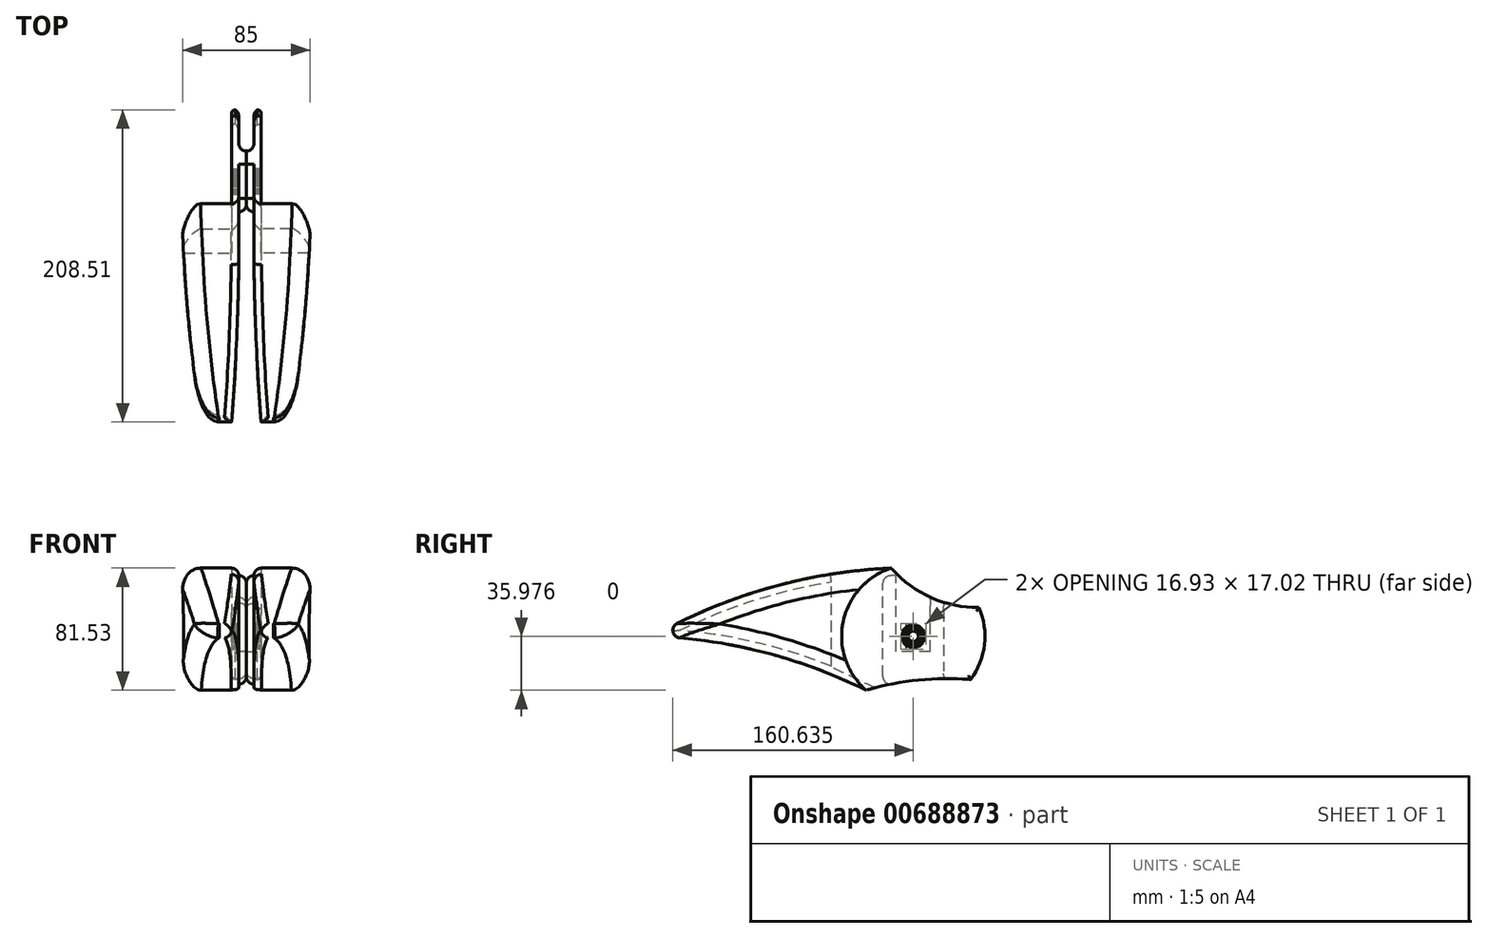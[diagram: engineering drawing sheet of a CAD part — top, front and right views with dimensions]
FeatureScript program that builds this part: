
annotation { "Feature Type Name" : "Feature", "Feature Type Description" : "" }
export const myFeature = defineFeature(function(context is Context, id is Id, definition is map)
    precondition{}
    {
        {
            var Q0;
            Q0=qCreatedBy(makeId("Right.planeOp"),FACE);
            var sketch = newSketch(context, id + "F0", { "sketchPlane" : qUnion([Q0])});
            skArc(sketch, "E0.0", {"start": v(-15.25, 45.51) * mm, "mid": v(-47.42, 9.65) * mm, "end": v(-32.12, -36.02) * mm});
            skArc(sketch, "E1", {"start": v(-15.25, 45.51) * mm, "mid": v(-97.5, 32.14) * mm, "end": v(-174.4, 0) * mm});
            skArc(sketch, "E2", {"start": v(-32.12, -36.02) * mm, "mid": v(-101.34, -10.43) * mm, "end": v(-174.4, 0) * mm});
            skArc(sketch, "E3", {"start": v(37.7, -28.86) * mm, "mid": v(2.47, -29.33) * mm, "end": v(-32.12, -36.02) * mm});
            skArc(sketch, "E4", {"start": v(-15.25, 45.51) * mm, "mid": v(11.16, 25.94) * mm, "end": v(43.33, 19.14) * mm});
            skArc(sketch, "E5.trimOffspring", {"start": v(37.7, -28.86) * mm, "mid": v(47.01, -5.62) * mm, "end": v(43.33, 19.14) * mm});
            skCircle(sketch, "E6", {"center": v(-0.54, -0.04) * mm, "radius": 3.43 * mm});
            skLineSegment(sketch, "E7", {"start": v(-0.54, -0.04) * mm, "end": v(-0.54, 10.9) * mm, "construction": true});
            skLineSegment(sketch, "E8.bottom", {"start": v(-0.55, 3.38) * mm, "end": v(-0.52, 3.38) * mm});
            skLineSegment(sketch, "E8.top", {"start": v(-0.55, 8.46) * mm, "end": v(-0.52, 8.46) * mm});
            skLineSegment(sketch, "E8.left", {"start": v(-0.55, 3.38) * mm, "end": v(-0.55, 8.46) * mm});
            skLineSegment(sketch, "E8.right", {"start": v(-0.52, 3.38) * mm, "end": v(-0.52, 8.46) * mm});
            skLineSegment(sketch, "E9.1.0", {"start": v(-1.24, 3.31) * mm, "end": v(-2.3, 8.28) * mm});
            skLineSegment(sketch, "E9.1.1", {"start": v(-1.26, 3.3) * mm, "end": v(-2.32, 8.28) * mm});
            skLineSegment(sketch, "E9.1.2", {"start": v(-2.32, 8.28) * mm, "end": v(-2.3, 8.28) * mm});
            skLineSegment(sketch, "E9.1.3", {"start": v(-1.26, 3.3) * mm, "end": v(-1.24, 3.31) * mm});
            skLineSegment(sketch, "E9.2.0", {"start": v(-1.92, 3.1) * mm, "end": v(-3.98, 7.73) * mm});
            skLineSegment(sketch, "E9.2.1", {"start": v(-1.94, 3.08) * mm, "end": v(-4, 7.72) * mm});
            skLineSegment(sketch, "E9.2.2", {"start": v(-4, 7.72) * mm, "end": v(-3.98, 7.73) * mm});
            skLineSegment(sketch, "E9.2.3", {"start": v(-1.94, 3.08) * mm, "end": v(-1.92, 3.1) * mm});
            skLineSegment(sketch, "E9.3.0", {"start": v(-2.54, 2.74) * mm, "end": v(-5.53, 6.85) * mm});
            skLineSegment(sketch, "E9.3.1", {"start": v(-2.56, 2.72) * mm, "end": v(-5.55, 6.83) * mm});
            skLineSegment(sketch, "E9.3.2", {"start": v(-5.55, 6.83) * mm, "end": v(-5.53, 6.85) * mm});
            skLineSegment(sketch, "E9.3.3", {"start": v(-2.56, 2.72) * mm, "end": v(-2.54, 2.74) * mm});
            skLineSegment(sketch, "E9.4.0", {"start": v(-3.08, 2.26) * mm, "end": v(-6.85, 5.66) * mm});
            skLineSegment(sketch, "E9.4.1", {"start": v(-3.1, 2.24) * mm, "end": v(-6.87, 5.64) * mm});
            skLineSegment(sketch, "E9.4.2", {"start": v(-6.87, 5.64) * mm, "end": v(-6.85, 5.66) * mm});
            skLineSegment(sketch, "E9.4.3", {"start": v(-3.1, 2.24) * mm, "end": v(-3.08, 2.26) * mm});
            skLineSegment(sketch, "E9.5.0", {"start": v(-3.5, 1.68) * mm, "end": v(-7.9, 4.22) * mm});
            skLineSegment(sketch, "E9.5.1", {"start": v(-3.51, 1.66) * mm, "end": v(-7.91, 4.2) * mm});
            skLineSegment(sketch, "E9.5.2", {"start": v(-7.91, 4.2) * mm, "end": v(-7.9, 4.22) * mm});
            skLineSegment(sketch, "E9.5.3", {"start": v(-3.51, 1.66) * mm, "end": v(-3.5, 1.68) * mm});
            skLineSegment(sketch, "E9.6.0", {"start": v(-3.8, 1.03) * mm, "end": v(-8.62, 2.6) * mm});
            skLineSegment(sketch, "E9.6.1", {"start": v(-3.8, 1) * mm, "end": v(-8.63, 2.57) * mm});
            skLineSegment(sketch, "E9.6.2", {"start": v(-8.63, 2.57) * mm, "end": v(-8.62, 2.6) * mm});
            skLineSegment(sketch, "E9.6.3", {"start": v(-3.8, 1) * mm, "end": v(-3.8, 1.03) * mm});
            skLineSegment(sketch, "E9.7.0", {"start": v(-3.94, 0.33) * mm, "end": v(-9, 0.86) * mm});
            skLineSegment(sketch, "E9.7.1", {"start": v(-3.95, 0.3) * mm, "end": v(-9, 0.83) * mm});
            skLineSegment(sketch, "E9.7.2", {"start": v(-9, 0.83) * mm, "end": v(-9, 0.86) * mm});
            skLineSegment(sketch, "E9.7.3", {"start": v(-3.95, 0.3) * mm, "end": v(-3.94, 0.33) * mm});
            skLineSegment(sketch, "E9.8.0", {"start": v(-3.95, -0.39) * mm, "end": v(-9, -0.92) * mm});
            skLineSegment(sketch, "E9.8.1", {"start": v(-3.94, -0.42) * mm, "end": v(-9, -0.95) * mm});
            skLineSegment(sketch, "E9.8.2", {"start": v(-9, -0.95) * mm, "end": v(-9, -0.92) * mm});
            skLineSegment(sketch, "E9.8.3", {"start": v(-3.94, -0.42) * mm, "end": v(-3.95, -0.39) * mm});
            skLineSegment(sketch, "E9.9.0", {"start": v(-3.8, -1.1) * mm, "end": v(-8.63, -2.66) * mm});
            skLineSegment(sketch, "E9.9.1", {"start": v(-3.8, -1.12) * mm, "end": v(-8.62, -2.69) * mm});
            skLineSegment(sketch, "E9.9.2", {"start": v(-8.62, -2.69) * mm, "end": v(-8.63, -2.66) * mm});
            skLineSegment(sketch, "E9.9.3", {"start": v(-3.8, -1.12) * mm, "end": v(-3.8, -1.1) * mm});
            skLineSegment(sketch, "E10.3.10.0", {"start": v(-3.5, -1.77) * mm, "end": v(-7.9, -4.3) * mm});
            skLineSegment(sketch, "E10.4.10.0", {"start": v(-3.51, -1.75) * mm, "end": v(-7.91, -4.29) * mm});
            skLineSegment(sketch, "E10.6.10.0", {"start": v(-7.9, -4.3) * mm, "end": v(-7.91, -4.29) * mm});
            skLineSegment(sketch, "E10.9.10.0", {"start": v(-3.5, -1.77) * mm, "end": v(-3.51, -1.75) * mm});
            skLineSegment(sketch, "E11.3.11.0", {"start": v(-3.08, -2.35) * mm, "end": v(-6.85, -5.75) * mm});
            skLineSegment(sketch, "E11.4.11.0", {"start": v(-3.1, -2.33) * mm, "end": v(-6.87, -5.73) * mm});
            skLineSegment(sketch, "E11.6.11.0", {"start": v(-6.85, -5.75) * mm, "end": v(-6.87, -5.73) * mm});
            skLineSegment(sketch, "E11.9.11.0", {"start": v(-3.08, -2.35) * mm, "end": v(-3.1, -2.33) * mm});
            skLineSegment(sketch, "E12.3.12.0", {"start": v(-2.54, -2.83) * mm, "end": v(-5.53, -6.94) * mm});
            skLineSegment(sketch, "E12.4.12.0", {"start": v(-2.56, -2.81) * mm, "end": v(-5.55, -6.92) * mm});
            skLineSegment(sketch, "E12.6.12.0", {"start": v(-5.53, -6.94) * mm, "end": v(-5.55, -6.92) * mm});
            skLineSegment(sketch, "E12.9.12.0", {"start": v(-2.54, -2.83) * mm, "end": v(-2.56, -2.81) * mm});
            skLineSegment(sketch, "E13.3.13.0", {"start": v(-1.92, -3.18) * mm, "end": v(-3.98, -7.82) * mm});
            skLineSegment(sketch, "E13.4.13.0", {"start": v(-1.94, -3.17) * mm, "end": v(-4, -7.81) * mm});
            skLineSegment(sketch, "E13.6.13.0", {"start": v(-3.98, -7.82) * mm, "end": v(-4, -7.81) * mm});
            skLineSegment(sketch, "E13.9.13.0", {"start": v(-1.92, -3.18) * mm, "end": v(-1.94, -3.17) * mm});
            skLineSegment(sketch, "E13.3.14.0", {"start": v(-1.24, -3.4) * mm, "end": v(-2.3, -8.37) * mm});
            skLineSegment(sketch, "E13.4.14.0", {"start": v(-1.26, -3.4) * mm, "end": v(-2.32, -8.36) * mm});
            skLineSegment(sketch, "E13.6.14.0", {"start": v(-2.3, -8.37) * mm, "end": v(-2.32, -8.36) * mm});
            skLineSegment(sketch, "E13.9.14.0", {"start": v(-1.24, -3.4) * mm, "end": v(-1.26, -3.4) * mm});
            skLineSegment(sketch, "E14.3.15.0", {"start": v(-0.52, -3.47) * mm, "end": v(-0.52, -8.55) * mm});
            skLineSegment(sketch, "E14.4.15.0", {"start": v(-0.55, -3.47) * mm, "end": v(-0.55, -8.55) * mm});
            skLineSegment(sketch, "E14.6.15.0", {"start": v(-0.52, -8.55) * mm, "end": v(-0.55, -8.55) * mm});
            skLineSegment(sketch, "E14.9.15.0", {"start": v(-0.52, -3.47) * mm, "end": v(-0.55, -3.47) * mm});
            skLineSegment(sketch, "E14.3.16.0", {"start": v(0.2, -3.4) * mm, "end": v(1.25, -8.36) * mm});
            skLineSegment(sketch, "E14.4.16.0", {"start": v(0.17, -3.4) * mm, "end": v(1.22, -8.37) * mm});
            skLineSegment(sketch, "E14.6.16.0", {"start": v(1.25, -8.36) * mm, "end": v(1.22, -8.37) * mm});
            skLineSegment(sketch, "E14.9.16.0", {"start": v(0.2, -3.4) * mm, "end": v(0.17, -3.4) * mm});
            skLineSegment(sketch, "E14.3.17.0", {"start": v(0.87, -3.17) * mm, "end": v(2.94, -7.81) * mm});
            skLineSegment(sketch, "E14.4.17.0", {"start": v(0.85, -3.18) * mm, "end": v(2.91, -7.82) * mm});
            skLineSegment(sketch, "E14.6.17.0", {"start": v(2.94, -7.81) * mm, "end": v(2.91, -7.82) * mm});
            skLineSegment(sketch, "E14.9.17.0", {"start": v(0.87, -3.17) * mm, "end": v(0.85, -3.18) * mm});
            skLineSegment(sketch, "E14.3.18.0", {"start": v(1.5, -2.81) * mm, "end": v(4.48, -6.92) * mm});
            skLineSegment(sketch, "E14.4.18.0", {"start": v(1.47, -2.83) * mm, "end": v(4.46, -6.94) * mm});
            skLineSegment(sketch, "E14.6.18.0", {"start": v(4.48, -6.92) * mm, "end": v(4.46, -6.94) * mm});
            skLineSegment(sketch, "E14.9.18.0", {"start": v(1.5, -2.81) * mm, "end": v(1.47, -2.83) * mm});
            skLineSegment(sketch, "E14.3.19.0", {"start": v(2.02, -2.33) * mm, "end": v(5.8, -5.73) * mm});
            skLineSegment(sketch, "E14.4.19.0", {"start": v(2, -2.35) * mm, "end": v(5.78, -5.75) * mm});
            skLineSegment(sketch, "E14.6.19.0", {"start": v(5.8, -5.73) * mm, "end": v(5.78, -5.75) * mm});
            skLineSegment(sketch, "E14.9.19.0", {"start": v(2.02, -2.33) * mm, "end": v(2, -2.35) * mm});
            skLineSegment(sketch, "E15.3.20.0", {"start": v(2.44, -1.75) * mm, "end": v(6.84, -4.29) * mm});
            skLineSegment(sketch, "E15.4.20.0", {"start": v(2.43, -1.77) * mm, "end": v(6.83, -4.3) * mm});
            skLineSegment(sketch, "E15.6.20.0", {"start": v(6.84, -4.29) * mm, "end": v(6.83, -4.3) * mm});
            skLineSegment(sketch, "E15.9.20.0", {"start": v(2.44, -1.75) * mm, "end": v(2.43, -1.77) * mm});
            skLineSegment(sketch, "E15.3.21.0", {"start": v(2.73, -1.1) * mm, "end": v(7.56, -2.66) * mm});
            skLineSegment(sketch, "E15.4.21.0", {"start": v(2.72, -1.12) * mm, "end": v(7.55, -2.69) * mm});
            skLineSegment(sketch, "E15.6.21.0", {"start": v(7.56, -2.66) * mm, "end": v(7.55, -2.69) * mm});
            skLineSegment(sketch, "E15.9.21.0", {"start": v(2.73, -1.1) * mm, "end": v(2.72, -1.12) * mm});
            skLineSegment(sketch, "E15.3.22.0", {"start": v(2.88, -0.39) * mm, "end": v(7.93, -0.92) * mm});
            skLineSegment(sketch, "E15.4.22.0", {"start": v(2.87, -0.42) * mm, "end": v(7.93, -0.95) * mm});
            skLineSegment(sketch, "E15.6.22.0", {"start": v(7.93, -0.92) * mm, "end": v(7.93, -0.95) * mm});
            skLineSegment(sketch, "E15.9.22.0", {"start": v(2.88, -0.39) * mm, "end": v(2.87, -0.42) * mm});
            skLineSegment(sketch, "E15.3.23.0", {"start": v(2.87, 0.33) * mm, "end": v(7.93, 0.86) * mm});
            skLineSegment(sketch, "E15.4.23.0", {"start": v(2.88, 0.3) * mm, "end": v(7.93, 0.83) * mm});
            skLineSegment(sketch, "E15.6.23.0", {"start": v(7.93, 0.86) * mm, "end": v(7.93, 0.83) * mm});
            skLineSegment(sketch, "E15.9.23.0", {"start": v(2.87, 0.33) * mm, "end": v(2.88, 0.3) * mm});
            skLineSegment(sketch, "E15.3.24.0", {"start": v(2.72, 1.03) * mm, "end": v(7.55, 2.6) * mm});
            skLineSegment(sketch, "E15.4.24.0", {"start": v(2.73, 1) * mm, "end": v(7.56, 2.57) * mm});
            skLineSegment(sketch, "E15.6.24.0", {"start": v(7.55, 2.6) * mm, "end": v(7.56, 2.57) * mm});
            skLineSegment(sketch, "E15.9.24.0", {"start": v(2.72, 1.03) * mm, "end": v(2.73, 1) * mm});
            skLineSegment(sketch, "E16.3.25.0", {"start": v(2.43, 1.68) * mm, "end": v(6.83, 4.22) * mm});
            skLineSegment(sketch, "E16.4.25.0", {"start": v(2.44, 1.66) * mm, "end": v(6.84, 4.2) * mm});
            skLineSegment(sketch, "E16.6.25.0", {"start": v(6.83, 4.22) * mm, "end": v(6.84, 4.2) * mm});
            skLineSegment(sketch, "E16.9.25.0", {"start": v(2.43, 1.68) * mm, "end": v(2.44, 1.66) * mm});
            skLineSegment(sketch, "E16.3.26.0", {"start": v(2, 2.26) * mm, "end": v(5.78, 5.66) * mm});
            skLineSegment(sketch, "E16.4.26.0", {"start": v(2.02, 2.24) * mm, "end": v(5.8, 5.64) * mm});
            skLineSegment(sketch, "E16.6.26.0", {"start": v(5.78, 5.66) * mm, "end": v(5.8, 5.64) * mm});
            skLineSegment(sketch, "E16.9.26.0", {"start": v(2, 2.26) * mm, "end": v(2.02, 2.24) * mm});
            skLineSegment(sketch, "E16.3.27.0", {"start": v(1.47, 2.74) * mm, "end": v(4.46, 6.85) * mm});
            skLineSegment(sketch, "E16.4.27.0", {"start": v(1.5, 2.72) * mm, "end": v(4.48, 6.83) * mm});
            skLineSegment(sketch, "E16.6.27.0", {"start": v(4.46, 6.85) * mm, "end": v(4.48, 6.83) * mm});
            skLineSegment(sketch, "E16.9.27.0", {"start": v(1.47, 2.74) * mm, "end": v(1.5, 2.72) * mm});
            skLineSegment(sketch, "E16.3.28.0", {"start": v(0.85, 3.1) * mm, "end": v(2.91, 7.73) * mm});
            skLineSegment(sketch, "E16.4.28.0", {"start": v(0.87, 3.08) * mm, "end": v(2.94, 7.72) * mm});
            skLineSegment(sketch, "E16.6.28.0", {"start": v(2.91, 7.73) * mm, "end": v(2.94, 7.72) * mm});
            skLineSegment(sketch, "E16.9.28.0", {"start": v(0.85, 3.1) * mm, "end": v(0.87, 3.08) * mm});
            skLineSegment(sketch, "E16.3.29.0", {"start": v(0.17, 3.31) * mm, "end": v(1.22, 8.28) * mm});
            skLineSegment(sketch, "E16.4.29.0", {"start": v(0.2, 3.3) * mm, "end": v(1.25, 8.28) * mm});
            skLineSegment(sketch, "E16.6.29.0", {"start": v(1.22, 8.28) * mm, "end": v(1.25, 8.28) * mm});
            skLineSegment(sketch, "E16.9.29.0", {"start": v(0.17, 3.31) * mm, "end": v(0.2, 3.3) * mm});
            skSolve(sketch);
        }
        {
            var Q0;
            Q0=makeQuery(id+"F0.imprint","IMPRINT",FACE,{"disambiguationData":[TD([[makeQuery(id+"F0.imprint","IMPRINT",EDGE,{"derivedFrom":sQuery(id+"F0.wireOp",EDGE,"E0.0")}),1.0]])]});
            extrude(context, id + "F1", {"entities" : qUnion([Q0]), "depth" : 4.83 * mm, "offsetDistance" : 25.4 * mm});
        }
        {
            var Q0;
            Q0=makeQuery(id+"F0.imprint","IMPRINT",FACE,{"disambiguationData":[TD([[makeQuery(id+"F0.imprint","IMPRINT",EDGE,{"derivedFrom":sQuery(id+"F0.wireOp",EDGE,"E0.0")}),-1.0]])]});
            extrude(context, id + "F2", {"entities" : qUnion([Q0]), "operationType" : NewBodyOperationType.ADD, "depth" : 38.1 * mm, "offsetDistance" : 25.4 * mm});
        }
        {
            var Q0;
            Q0=makeQuery(id+"F1.opExtrude","CAP_EDGE",EDGE,{"disambiguationData":[OSD([sQuery(id+"F0.wireOp",EDGE,"E4")])],"isStart":false});
            var Q1;
            Q1=makeQuery(id+"F1.opExtrude","CAP_EDGE",EDGE,{"disambiguationData":[OSD([sQuery(id+"F0.wireOp",EDGE,"E3")])],"isStart":false});
            var Q2;
            Q2=makeQuery(id+"F1.opExtrude","CAP_EDGE",EDGE,{"disambiguationData":[OSD([sQuery(id+"F0.wireOp",EDGE,"E5.trimOffspring")])],"isStart":false});
            fillet(context, id + "F3", {"entities" : qUnion([Q0, Q1, Q2]), "radius" : 2.54 * mm, "tangentPropagation" : true, "allowEdgeOverflow" : false});
        }
        {
            var Q0;
            Q0=makeQuery(id+"F2.boolean.opBoolean","SPLIT",EDGE,{"derivedFrom":makeQuery(id+"F2.opExtrude","SWEPT_EDGE",EDGE,{"disambiguationData":[OSD([sQuery(id+"F0.wireOp",EDGE,"E0.0"),sQuery(id+"F0.wireOp",EDGE,"E1"),sQuery(id+"F0.wireOp",EDGE,"E4")])]})});
            cPlane(context, id + "F4", {"entities" : qUnion([Q0]), "cplaneType" : CPlaneType.LINE_ANGLE, "offset" : 0 * mm, "angle" : 90 * degree, "width" : 152.4 * mm, "height" : 152.4 * mm});
        }
        {
            var Q0;
            Q0=qCreatedBy(id+"F4.planeOp",FACE);
            var sketch = newSketch(context, id + "F5", { "sketchPlane" : qUnion([Q0])});
            skLineSegment(sketch, "E17", {"start": v(22.21, -178.45) * mm, "end": v(43.85, -178.45) * mm});
            skLineSegment(sketch, "E18", {"start": v(43.85, -178.45) * mm, "end": v(43.85, -15.25) * mm});
            skLineSegment(sketch, "E19", {"start": v(43.85, -15.25) * mm, "end": v(38.1, -15.25) * mm});
            skArc(sketch, "E20", {"start": v(22.21, -178.45) * mm, "mid": v(33.2, -97.15) * mm, "end": v(38.1, -15.25) * mm});
            skArc(sketch, "E21", {"start": v(0, -15.25) * mm, "mid": v(0.95, -94.53) * mm, "end": v(5.71, -173.68) * mm});
            skLineSegment(sketch, "E22", {"start": v(0, -15.25) * mm, "end": v(-6.93, -15.25) * mm});
            skLineSegment(sketch, "E23", {"start": v(-6.93, -15.25) * mm, "end": v(-6.93, -180.22) * mm});
            skLineSegment(sketch, "E24", {"start": v(-6.93, -180.22) * mm, "end": v(5.71, -180.22) * mm});
            skLineSegment(sketch, "E25", {"start": v(5.71, -180.22) * mm, "end": v(5.71, -173.68) * mm});
            skSolve(sketch);
        }
        {
            var Q0;
            Q0=qSketchRegion(id+"F5",true);
            extrude(context, id + "F6", {"entities" : qUnion([Q0]), "operationType" : NewBodyOperationType.REMOVE, "endBound" : BoundingType.THROUGH_ALL, "oppositeDirection" : true, "depth" : 25.4 * mm, "offsetDistance" : 25.4 * mm});
        }
        {
            var Q0;
            Q0=makeQuery(id+"F6.boolean.opBoolean","INTERSECT",EDGE,{"derivedFrom":[makeQuery(id+"F2.opExtrude","SWEPT_FACE",FACE,{"disambiguationData":[OSD([sQuery(id+"F0.wireOp",EDGE,"E1")])]}),makeQuery(id+"F6.opExtrude","SWEPT_FACE",FACE,{"disambiguationData":[OSD([sQuery(id+"F5.wireOp",EDGE,"E20")])]})]});
            var Q1;
            Q1=makeQuery(id+"F6.boolean.opBoolean","INTERSECT",EDGE,{"derivedFrom":[makeQuery(id+"F2.opExtrude","SWEPT_FACE",FACE,{"disambiguationData":[OSD([sQuery(id+"F0.wireOp",EDGE,"E2")])]}),makeQuery(id+"F6.opExtrude","SWEPT_FACE",FACE,{"disambiguationData":[OSD([sQuery(id+"F5.wireOp",EDGE,"E20")])]})]});
            fillet(context, id + "F7", {"entities" : qUnion([Q0, Q1]), "radius" : 12.7 * mm, "tangentPropagation" : true, "allowEdgeOverflow" : false});
        }
        {
            var Q0;
            Q0=makeQuery(id+"F2.opExtrude","SWEPT_EDGE",EDGE,{"disambiguationData":[OSD([sQuery(id+"F0.wireOp",EDGE,"E1"),sQuery(id+"F0.wireOp",EDGE,"E2")])]});
            var Q1;
            Q1=makeQuery(id+"F6.boolean.opBoolean","INTERSECT",EDGE,{"derivedFrom":[makeQuery(id+"F2.opExtrude","SWEPT_FACE",FACE,{"disambiguationData":[OSD([sQuery(id+"F0.wireOp",EDGE,"E1")])]}),makeQuery(id+"F6.opExtrude","SWEPT_FACE",FACE,{"disambiguationData":[OSD([sQuery(id+"F5.wireOp",EDGE,"E21")])]})]});
            var Q2;
            Q2=makeQuery(id+"F6.boolean.opBoolean","INTERSECT",EDGE,{"derivedFrom":[makeQuery(id+"F2.opExtrude","SWEPT_FACE",FACE,{"disambiguationData":[OSD([sQuery(id+"F0.wireOp",EDGE,"E2")])]}),makeQuery(id+"F6.opExtrude","SWEPT_FACE",FACE,{"disambiguationData":[OSD([sQuery(id+"F5.wireOp",EDGE,"E21")])]})]});
            fillet(context, id + "F8", {"entities" : qUnion([Q0, Q1, Q2]), "radius" : 5.08 * mm, "tangentPropagation" : true, "allowEdgeOverflow" : false});
        }
        {
            var Q0;
            Q0=makeQuery(id+"F0.imprint","IMPRINT",FACE,{"disambiguationData":[TD([[makeQuery(id+"F0.imprint","IMPRINT",EDGE,{"derivedFrom":sQuery(id+"F0.wireOp",EDGE,"E0.0")}),1.0]])]});
            var sketch = newSketch(context, id + "F9", { "sketchPlane" : qUnion([Q0])});
            skCircle(sketch, "E26.0", {"center": v(-0.54, -0.04) * mm, "radius": 3.43 * mm});
            skArc(sketch, "E27.0", {"start": v(-15.25, 45.51) * mm, "mid": v(11.16, 25.94) * mm, "end": v(43.33, 19.14) * mm});
            skArc(sketch, "E28.0", {"start": v(37.7, -28.86) * mm, "mid": v(2.47, -29.33) * mm, "end": v(-32.12, -36.02) * mm});
            skLineSegment(sketch, "E29", {"start": v(19.78, 22.66) * mm, "end": v(19.78, -28.32) * mm});
            skArc(sketch, "E30.0", {"start": v(-55.2, 36.35) * mm, "mid": v(-32.95, 39.2) * mm, "end": v(-10.56, 40.6) * mm});
            skLineSegment(sketch, "E31", {"start": v(-20.86, -33.14) * mm, "end": v(-20.86, 40.13) * mm});
            skLineSegment(sketch, "E32.bottom", {"start": v(10.9, -10.2) * mm, "end": v(-11.97, -10.2) * mm});
            skLineSegment(sketch, "E32.top", {"start": v(10.9, 42.4) * mm, "end": v(-11.97, 42.4) * mm});
            skLineSegment(sketch, "E32.left", {"start": v(10.9, -10.2) * mm, "end": v(10.9, 42.4) * mm});
            skLineSegment(sketch, "E32.right", {"start": v(-11.97, -10.2) * mm, "end": v(-11.97, 42.4) * mm});
            skSolve(sketch);
        }
        {
            var Q0;
            {var subQ4=sQuery(id+"F9.wireOp",EDGE,"E29");Q0=makeQuery(id+"F9.imprint","IMPRINT",FACE,{"disambiguationData":[TD([[makeQuery(id+"F9.imprint","IMPRINT",EDGE,{"derivedFrom":subQ4}),-1.0]])]});}
            extrude(context, id + "F10", {"entities" : qUnion([Q0]), "operationType" : NewBodyOperationType.ADD, "oppositeDirection" : true, "depth" : 5.08 * mm, "offsetDistance" : 25.4 * mm});
        }
        {
            var Q0;
            Q0=makeQuery(id+"F10.opExtrude","CAP_EDGE",EDGE,{"disambiguationData":[OSD([sQuery(id+"F9.wireOp",EDGE,"E29")])],"isStart":true});
            var Q1;
            Q1=makeQuery(id+"F10.opExtrude","CAP_EDGE",EDGE,{"disambiguationData":[OSD([sQuery(id+"F9.wireOp",EDGE,"E31")])],"isStart":false});
            fillet(context, id + "F11", {"entities" : qUnion([Q0, Q1]), "radius" : 5.08 * mm, "tangentPropagation" : true, "allowEdgeOverflow" : false});
        }
        {
            var Q0;
            Q0=makeQuery(id+"F1.opExtrude","CAP_EDGE",EDGE,{"disambiguationData":[OSD([sQuery(id+"F0.wireOp",EDGE,"E5.trimOffspring")])],"isStart":true});
            var Q1;
            Q1=makeQuery(id+"F10.opExtrude","CAP_EDGE",EDGE,{"disambiguationData":[OSD([sQuery(id+"F9.wireOp",EDGE,"E28.0")])],"isStart":false});
            var Q2;
            Q2=makeQuery(id+"F10.opExtrude","CAP_EDGE",EDGE,{"disambiguationData":[OSD([sQuery(id+"F9.wireOp",EDGE,"E27.0")])],"isStart":false});
            var Q3;
            Q3=makeQuery(id+"F10.opExtrude","CAP_EDGE",EDGE,{"disambiguationData":[OSD([sQuery(id+"F9.wireOp",EDGE,"E30.0")])],"isStart":false});
            fillet(context, id + "F12", {"entities" : qUnion([Q0, Q1, Q2, Q3]), "radius" : 5.08 * mm, "tangentPropagation" : true, "allowEdgeOverflow" : false});
        }
        {
            var Q0;
            Q0=makeQuery(id+"F10.opExtrude","CAP_FACE",FACE,{"disambiguationData":[OSD([sQuery(id+"F9.wireOp",EDGE,"E27.0"),sQuery(id+"F9.wireOp",EDGE,"E28.0"),sQuery(id+"F9.wireOp",EDGE,"E29"),sQuery(id+"F9.wireOp",EDGE,"E30.0"),sQuery(id+"F9.wireOp",EDGE,"E31"),sQuery(id+"F9.wireOp",EDGE,"E32.bottom"),sQuery(id+"F9.wireOp",EDGE,"E32.left"),sQuery(id+"F9.wireOp",EDGE,"E32.right")])],"isStart":false});
            cPlane(context, id + "F13", {"entities" : qUnion([Q0]), "cplaneType" : CPlaneType.OFFSET, "offset" : 0 * mm, "width" : 152.4 * mm, "height" : 152.4 * mm});
        }
        {
            var Q0;
            Q0=makeQuery(id+"F1.opExtrude","SWEPT_BODY",BODY,{"disambiguationData":[OSD([sQuery(id+"F0.wireOp",EDGE,"E0.0"),sQuery(id+"F0.wireOp",EDGE,"E3"),sQuery(id+"F0.wireOp",EDGE,"E4"),sQuery(id+"F0.wireOp",EDGE,"E5.trimOffspring"),sQuery(id+"F0.wireOp",EDGE,"E6"),sQuery(id+"F0.wireOp",EDGE,"E8.top"),sQuery(id+"F0.wireOp",EDGE,"E8.left"),sQuery(id+"F0.wireOp",EDGE,"E8.right"),sQuery(id+"F0.wireOp",EDGE,"E9.1.0"),sQuery(id+"F0.wireOp",EDGE,"E9.1.1"),sQuery(id+"F0.wireOp",EDGE,"E9.1.2"),sQuery(id+"F0.wireOp",EDGE,"E9.2.0"),sQuery(id+"F0.wireOp",EDGE,"E9.2.1"),sQuery(id+"F0.wireOp",EDGE,"E9.2.2"),sQuery(id+"F0.wireOp",EDGE,"E9.3.0"),sQuery(id+"F0.wireOp",EDGE,"E9.3.1"),sQuery(id+"F0.wireOp",EDGE,"E9.3.2"),sQuery(id+"F0.wireOp",EDGE,"E9.4.0"),sQuery(id+"F0.wireOp",EDGE,"E9.4.1"),sQuery(id+"F0.wireOp",EDGE,"E9.4.2"),sQuery(id+"F0.wireOp",EDGE,"E9.5.0"),sQuery(id+"F0.wireOp",EDGE,"E9.5.1"),sQuery(id+"F0.wireOp",EDGE,"E9.5.2"),sQuery(id+"F0.wireOp",EDGE,"E9.6.0"),sQuery(id+"F0.wireOp",EDGE,"E9.6.1"),sQuery(id+"F0.wireOp",EDGE,"E9.6.2"),sQuery(id+"F0.wireOp",EDGE,"E9.7.0"),sQuery(id+"F0.wireOp",EDGE,"E9.7.1"),sQuery(id+"F0.wireOp",EDGE,"E9.7.2"),sQuery(id+"F0.wireOp",EDGE,"E9.8.0"),sQuery(id+"F0.wireOp",EDGE,"E9.8.1"),sQuery(id+"F0.wireOp",EDGE,"E9.8.2"),sQuery(id+"F0.wireOp",EDGE,"E9.9.0"),sQuery(id+"F0.wireOp",EDGE,"E9.9.1"),sQuery(id+"F0.wireOp",EDGE,"E9.9.2"),sQuery(id+"F0.wireOp",EDGE,"E10.3.10.0"),sQuery(id+"F0.wireOp",EDGE,"E10.4.10.0"),sQuery(id+"F0.wireOp",EDGE,"E10.6.10.0"),sQuery(id+"F0.wireOp",EDGE,"E11.3.11.0"),sQuery(id+"F0.wireOp",EDGE,"E11.4.11.0"),sQuery(id+"F0.wireOp",EDGE,"E11.6.11.0"),sQuery(id+"F0.wireOp",EDGE,"E12.3.12.0"),sQuery(id+"F0.wireOp",EDGE,"E12.4.12.0"),sQuery(id+"F0.wireOp",EDGE,"E12.6.12.0"),sQuery(id+"F0.wireOp",EDGE,"E13.3.13.0"),sQuery(id+"F0.wireOp",EDGE,"E13.4.13.0"),sQuery(id+"F0.wireOp",EDGE,"E13.6.13.0"),sQuery(id+"F0.wireOp",EDGE,"E13.3.14.0"),sQuery(id+"F0.wireOp",EDGE,"E13.4.14.0"),sQuery(id+"F0.wireOp",EDGE,"E13.6.14.0"),sQuery(id+"F0.wireOp",EDGE,"E14.3.15.0"),sQuery(id+"F0.wireOp",EDGE,"E14.4.15.0"),sQuery(id+"F0.wireOp",EDGE,"E14.6.15.0"),sQuery(id+"F0.wireOp",EDGE,"E14.3.16.0"),sQuery(id+"F0.wireOp",EDGE,"E14.4.16.0"),sQuery(id+"F0.wireOp",EDGE,"E14.6.16.0"),sQuery(id+"F0.wireOp",EDGE,"E14.3.17.0"),sQuery(id+"F0.wireOp",EDGE,"E14.4.17.0"),sQuery(id+"F0.wireOp",EDGE,"E14.6.17.0"),sQuery(id+"F0.wireOp",EDGE,"E14.3.18.0"),sQuery(id+"F0.wireOp",EDGE,"E14.4.18.0"),sQuery(id+"F0.wireOp",EDGE,"E14.6.18.0"),sQuery(id+"F0.wireOp",EDGE,"E14.3.19.0"),sQuery(id+"F0.wireOp",EDGE,"E14.4.19.0"),sQuery(id+"F0.wireOp",EDGE,"E14.6.19.0"),sQuery(id+"F0.wireOp",EDGE,"E15.3.20.0"),sQuery(id+"F0.wireOp",EDGE,"E15.4.20.0"),sQuery(id+"F0.wireOp",EDGE,"E15.6.20.0"),sQuery(id+"F0.wireOp",EDGE,"E15.3.21.0"),sQuery(id+"F0.wireOp",EDGE,"E15.4.21.0"),sQuery(id+"F0.wireOp",EDGE,"E15.6.21.0"),sQuery(id+"F0.wireOp",EDGE,"E15.3.22.0"),sQuery(id+"F0.wireOp",EDGE,"E15.4.22.0"),sQuery(id+"F0.wireOp",EDGE,"E15.6.22.0"),sQuery(id+"F0.wireOp",EDGE,"E15.3.23.0"),sQuery(id+"F0.wireOp",EDGE,"E15.4.23.0"),sQuery(id+"F0.wireOp",EDGE,"E15.6.23.0"),sQuery(id+"F0.wireOp",EDGE,"E15.3.24.0"),sQuery(id+"F0.wireOp",EDGE,"E15.4.24.0"),sQuery(id+"F0.wireOp",EDGE,"E15.6.24.0"),sQuery(id+"F0.wireOp",EDGE,"E16.3.25.0"),sQuery(id+"F0.wireOp",EDGE,"E16.4.25.0"),sQuery(id+"F0.wireOp",EDGE,"E16.6.25.0"),sQuery(id+"F0.wireOp",EDGE,"E16.3.26.0"),sQuery(id+"F0.wireOp",EDGE,"E16.4.26.0"),sQuery(id+"F0.wireOp",EDGE,"E16.6.26.0"),sQuery(id+"F0.wireOp",EDGE,"E16.3.27.0"),sQuery(id+"F0.wireOp",EDGE,"E16.4.27.0"),sQuery(id+"F0.wireOp",EDGE,"E16.6.27.0"),sQuery(id+"F0.wireOp",EDGE,"E16.3.28.0"),sQuery(id+"F0.wireOp",EDGE,"E16.4.28.0"),sQuery(id+"F0.wireOp",EDGE,"E16.6.28.0"),sQuery(id+"F0.wireOp",EDGE,"E16.3.29.0"),sQuery(id+"F0.wireOp",EDGE,"E16.4.29.0"),sQuery(id+"F0.wireOp",EDGE,"E16.6.29.0")])]});
            var Q1;
            Q1=qCreatedBy(id+"F13.planeOp",FACE);
            mirror(context, id + "F14", {"entities" : qUnion([Q0]), "mirrorPlane" : qUnion([Q1])});
        }
    });
